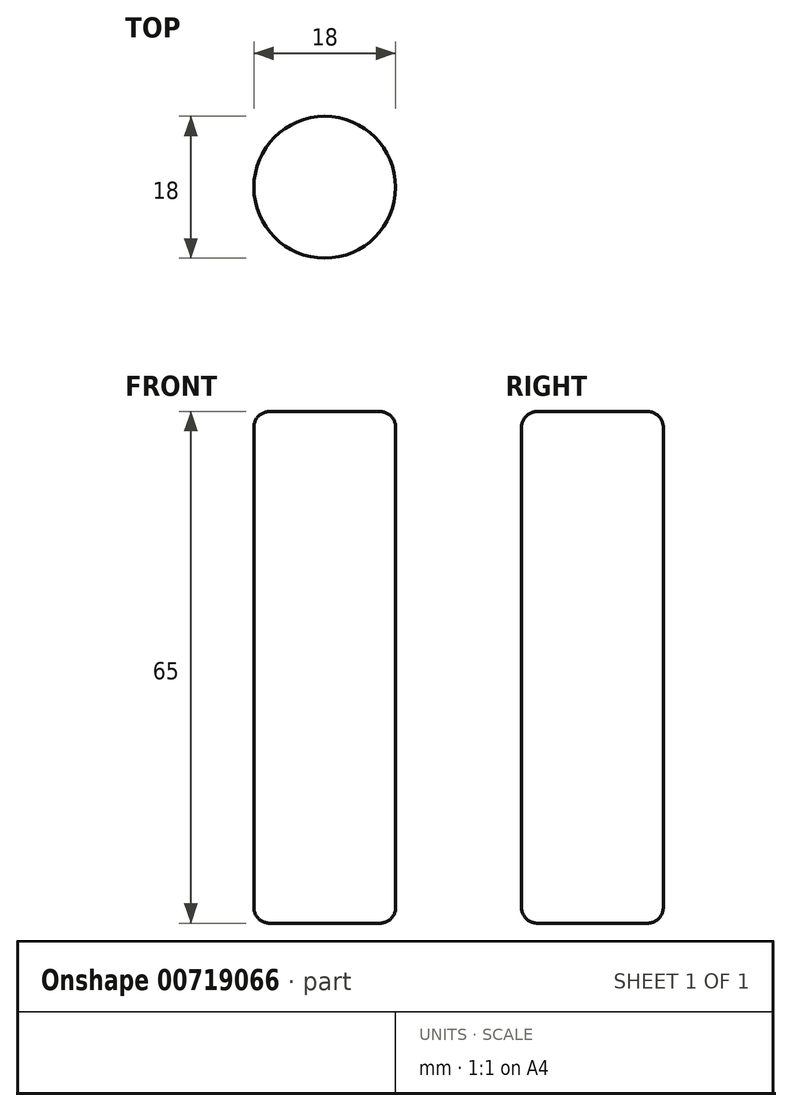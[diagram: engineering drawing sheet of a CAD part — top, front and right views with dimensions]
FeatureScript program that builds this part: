
annotation { "Feature Type Name" : "Feature", "Feature Type Description" : "" }
export const myFeature = defineFeature(function(context is Context, id is Id, definition is map)
    precondition{}
    {
        {
            var Q0;
            Q0=qCreatedBy(makeId("Top.planeOp"),FACE);
            var sketch = newSketch(context, id + "F0", { "sketchPlane" : qUnion([Q0])});
            skCircle(sketch, "E0", {"center": v(0, 0) * mm, "radius": 9 * mm});
            skSolve(sketch);
        }
        {
            var Q0;
            Q0=makeQuery(id+"F0.imprint","IMPRINT",FACE,{"disambiguationData":[TD([[makeQuery(id+"F0.imprint","IMPRINT",EDGE,{"derivedFrom":sQuery(id+"F0.wireOp",EDGE,"E0")}),1.0]])]});
            extrude(context, id + "F1", {"entities" : qUnion([Q0]), "depth" : 65 * mm, "offsetDistance" : 25 * mm});
        }
        {
            var Q0;
            Q0=makeQuery(id+"F1.opExtrude","CAP_EDGE",EDGE,{"disambiguationData":[OSD([sQuery(id+"F0.wireOp",EDGE,"E0")])],"isStart":true});
            var Q1;
            Q1=makeQuery(id+"F1.opExtrude","SWEPT_FACE",FACE,{"disambiguationData":[OSD([sQuery(id+"F0.wireOp",EDGE,"E0")])]});
            var Q2;
            Q2=makeQuery(id+"F1.opExtrude","CAP_EDGE",EDGE,{"disambiguationData":[OSD([sQuery(id+"F0.wireOp",EDGE,"E0")])],"isStart":false});
            var Q3;
            Q3=makeQuery(id+"F1.opExtrude","CAP_FACE",FACE,{"disambiguationData":[OSD([sQuery(id+"F0.wireOp",EDGE,"E0")])],"isStart":true});
            var Q4;
            Q4=makeQuery(id+"F1.opExtrude","CAP_FACE",FACE,{"disambiguationData":[OSD([sQuery(id+"F0.wireOp",EDGE,"E0")])],"isStart":false});
            fillet(context, id + "F2", {"entities" : qUnion([Q0, Q1, Q2, Q3, Q4]), "radius" : 2 * mm, "tangentPropagation" : true, "allowEdgeOverflow" : false});
        }
    });
